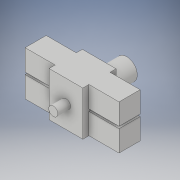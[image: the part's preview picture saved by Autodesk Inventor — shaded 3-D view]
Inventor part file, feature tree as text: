
AUTODESK INVENTOR PART (.ipt)
format: ipt  version: 2019 (Build 230136000, 136)  size: 147,968 bytes
history: native  units: mm
features: extrude x5, sketch x5
ambient origin geometry x8: Origin, YZ Plane, XZ Plane, XY Plane, X Axis, Y Axis, Z Axis, Center Point
bodies: Solid1 (feature_tree)
feature tree (10):
  extrude  "Extrusion1"  Depth=133.35mm
  extrude  "Extrusion2"  Depth=50.8mm
  extrude  "Extrusion3"  Depth=100.075mm
  extrude  "Extrusion4"  Depth=63.5mm
  extrude  "Extrusion5"  Depth=18.288mm
  sketch  "Sketch1"  dims[d1=101.6mm d2=133.35mm]
  sketch  "Sketch2"  dims[d3=66.75mm d4=50.8mm]
  sketch  "Sketch3"  dims[d5=100.075mm d6=0.0mm d7=27.25mm]
  sketch  "Sketch4"  dims[d8=38.1mm d9=0.0mm d10=63.5mm]
  sketch  "Sketch5"  dims[d11=82.55mm d12=0.0mm d13=18.288mm d14=18.288mm d15=63.499mm d16=63.499mm d17=63.499mm d18=90.424mm d19=0.0mm d20=90.424mm d21=0.0mm]
